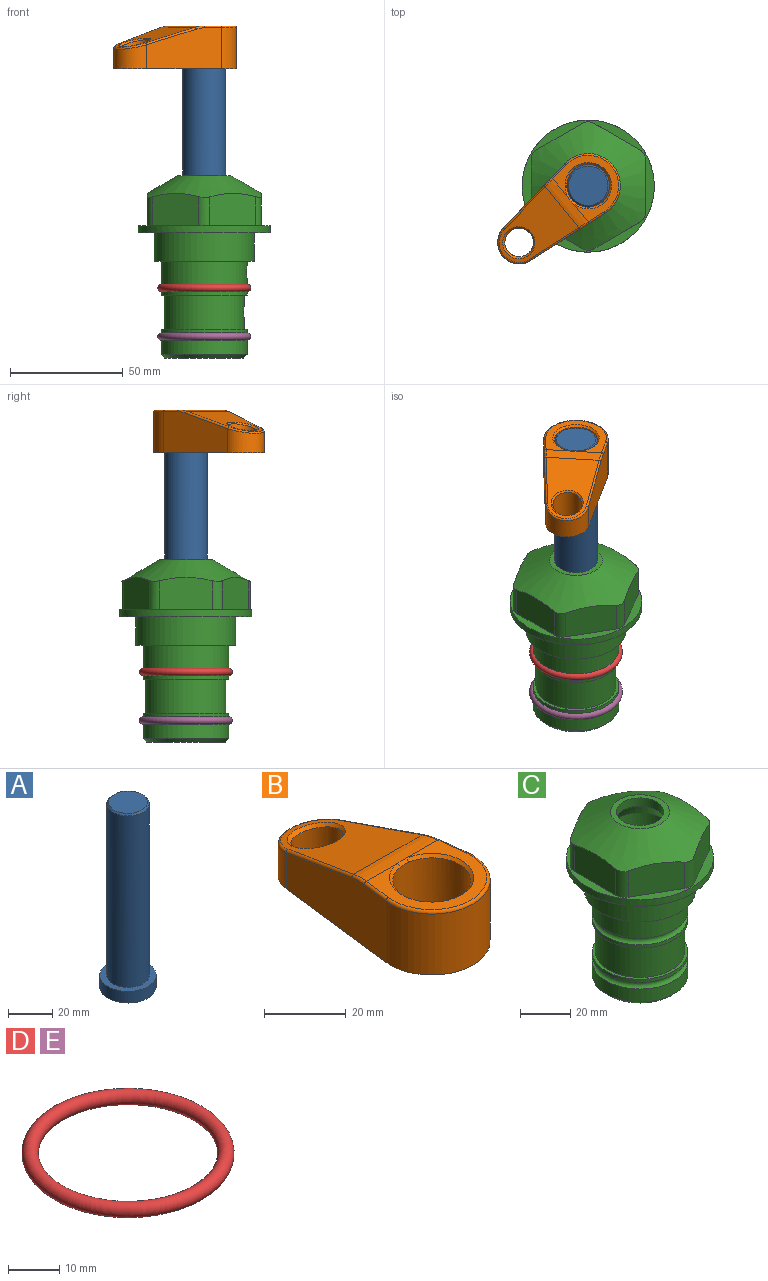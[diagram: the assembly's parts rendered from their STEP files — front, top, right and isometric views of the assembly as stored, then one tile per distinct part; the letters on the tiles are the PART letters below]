
ASSEMBLY  parts=5 mates=4
PART A: 6 faces, bbox 25.4x25.4x101.6 mm
  f0: plane 17.46x17.46mm, normal (0,0,1), area 239.5mm2, adj f5
  f1: plane 25.4x25.4mm, normal (0,0,-1), area 506.7mm2, adj f2
  f2: cylinder r=12.7mm len=25.4mm, axis (0,0,1), area 506.7mm2, adj f1,f3
  f3: plane 25.4x25.4mm, normal (0,0,1), area 221.7mm2, adj f2,f4
  f4: cylinder r=9.53mm len=94.46mm, axis (0,0,1), area 5653mm2, adj f3,f5
  f5: cone r=8.73mm half-angle=45deg, axis (0,0,-1), area 64.4mm2, adj f0,f4
PART B: 31 faces, bbox 31.7x65.5x19.8 mm
  f0: plane 39.12x18.26mm, normal (0.99,0.12,0), area 612.2mm2, adj f1,f4,f7,f11,f13,f15
  f1: cylinder r=9.53mm len=18.91mm, axis (0,0,-1), area 296.1mm2, adj f0,f2,f7,f17
  f2: plane 39.12x18.26mm, normal (-0.99,0.12,0), area 612.2mm2, adj f1,f4,f7,f12,f14,f16
  f3: cylinder r=6.35mm len=12.7mm, axis (0,0,-1), area 362.4mm2, adj f7,f18
  f4: cylinder r=14.29mm len=28.58mm, axis (0,0,-1), area 882.2mm2, adj f0,f2,f7,f10
  f5: cylinder r=9.53mm len=19.05mm, axis (0,0,-1), area 1092.6mm2, adj f7,f19,f20
  f6: plane 26.99x23.69mm, normal (0,0,1), area 216.2mm2, adj f9,f10,f11,f12,f19
  f7: plane 63.5x28.58mm, normal (0,0,-1), area 661.8mm2, adj f0,f1,f2,f3,f4,f5,f22,f23
  f8: plane 33.52x23.6mm, normal (0,0.26,0.97), area 486mm2, adj f9,f15,f16,f17,f18
  f9: cylinder r=19.05mm len=24.72mm, axis (1,0,0), area 120.4mm2, adj f6,f8,f13,f14,f20
  f10: torus R=13.49mm, axis (0,0,1), area 59mm2, adj f4,f6,f11,f12
  f11: cylinder r=0.79mm len=8.67mm, axis (0.12,-0.99,0), area 10.8mm2, adj f0,f6,f10,f13
  f12: cylinder r=0.79mm len=8.67mm, axis (0.12,0.99,0), area 10.8mm2, adj f2,f6,f10,f14
  f13: bspline ~4.95x1.42mm, area 6.1mm2, adj f0,f9,f11,f15
  f14: bspline ~4.95x1.42mm, area 6.1mm2, adj f2,f9,f12,f16
  f15: cylinder r=0.79mm len=25.95mm, axis (0.12,-0.96,0.26), area 32.9mm2, adj f0,f8,f13,f17
  f16: cylinder r=0.79mm len=25.95mm, axis (0.12,0.96,-0.26), area 32.9mm2, adj f2,f8,f14,f17
  f17: bspline ~18.91x8.38mm, area 30mm2, adj f1,f8,f15,f16
  f18: bspline ~14.29x14.29mm, area 48.3mm2, adj f3,f8
  f19: cone r=9.53mm half-angle=45deg, axis (0,0,1), area 66.5mm2, adj f5,f6,f20
  f20: bspline ~3.22x0.96mm, area 3.5mm2, adj f5,f9,f19
  f21: plane 2.75x2.72mm, normal (0,0,-1), area 2.9mm2, adj f23,f25,f28
  f22: plane 23.05x15.88mm, normal (-0.99,-0.12,0), area 323.6mm2, adj f7,f25,f26,f27,f28,f29
  f23: plane 23.05x15.88mm, normal (0.99,-0.12,0), area 323.6mm2, adj f7,f21,f25,f27,f28,f30
  f24: cylinder r=9.53mm len=10.69mm, axis (0,0,-1), area 114.7mm2, adj f7,f27,f29,f30
  f25: cylinder r=12.7mm len=20.59mm, axis (0,0,-1), area 381.1mm2, adj f7,f21,f22,f23,f26,f28
  f26: plane 2.75x2.72mm, normal (0,0,-1), area 2.9mm2, adj f22,f25,f28
  f27: plane 19.72x18.37mm, normal (0,-0.26,-0.97), area 291.8mm2, adj f22,f23,f24,f28,f29,f30
  f28: cylinder r=15.88mm len=19.92mm, axis (1,0,0), area 54.8mm2, adj f21,f22,f23,f25,f26,f27
  f29: cylinder r=1.59mm len=11mm, axis (0,0,-1), area 34.7mm2, adj f7,f22,f24,f27
  f30: cylinder r=1.59mm len=11mm, axis (0,0,-1), area 34.7mm2, adj f7,f23,f24,f27
PART C: 36 faces, bbox 58.7x58.7x81 mm
  f0: cylinder r=17.78mm len=35.56mm, axis (0,0,1), area 1670.8mm2, adj f23,f24,f31
  f1: cylinder r=19.05mm len=38.1mm, axis (0,0,1), area 1191.9mm2, adj f26,f27,f30
  f2: plane 58.66x58.66mm, normal (0,0,-1), area 1150.6mm2, adj f3,f28
  f3: cylinder r=29.33mm len=58.66mm, axis (0,0,-1), area 585.1mm2, adj f2,f4
  f4: plane 58.66x58.66mm, normal (0,0,1), area 475.9mm2, adj f3,f5,f6,f7,f8,f9,f10,f11
  f5: plane 20.32x14.34mm, normal (-0.5,0.87,0), area 324.4mm2, adj f4,f15,f16,f17
  f6: plane 20.32x14.34mm, normal (0.5,0.87,0), area 324.4mm2, adj f4,f14,f15,f17
  f7: plane 23.48x14.34mm, normal (1,0,0), area 324.4mm2, adj f4,f13,f14,f17
  f8: plane 20.32x14.34mm, normal (0.5,-0.87,0), area 324.4mm2, adj f4,f12,f13,f17
  f9: plane 20.32x14.34mm, normal (-0.5,-0.87,0), area 324.4mm2, adj f4,f11,f12,f17
  f10: plane 23.48x14.34mm, normal (-1,0,0), area 324.4mm2, adj f4,f11,f16,f17
  f11: cylinder r=5.08mm len=12.85mm, axis (0,0,-1), area 67.2mm2, adj f4,f9,f10,f17
  f12: cylinder r=5.08mm len=12.85mm, axis (0,0,-1), area 67.2mm2, adj f4,f8,f9,f17
  f13: cylinder r=5.08mm len=12.85mm, axis (0,0,-1), area 67.2mm2, adj f4,f7,f8,f17
  f14: cylinder r=5.08mm len=12.85mm, axis (0,0,-1), area 67.2mm2, adj f4,f6,f7,f17
  f15: cylinder r=5.08mm len=12.85mm, axis (0,0,-1), area 67.2mm2, adj f4,f5,f6,f17
  f16: cylinder r=5.08mm len=12.85mm, axis (0,0,-1), area 67.2mm2, adj f4,f5,f10,f17
  f17: cone r=11.73mm half-angle=60deg, axis (0,0,-1), area 2071.8mm2, adj f5,f6,f7,f8,f9,f10,f11,f12
  f18: plane 23.46x23.46mm, normal (0,0,1), area 147.4mm2, adj f17,f35
  f19: plane 34.93x34.93mm, normal (0,0,-1), area 958mm2, adj f29
  f20: cylinder r=19.05mm len=38.1mm, axis (0,0,1), area 760.1mm2, adj f21,f29
  f21: torus R=19.05mm, axis (0,0,1), area 565.3mm2, adj f20,f22
  f22: cylinder r=19.05mm len=38.1mm, axis (0,0,1), area 190mm2, adj f21,f23
  f23: plane 38.1x38.1mm, normal (0,0,1), area 146.9mm2, adj f0,f22
  f24: plane 38.1x38.1mm, normal (0,0,-1), area 146.9mm2, adj f0,f25
  f25: cylinder r=19.05mm len=38.1mm, axis (0,0,1), area 190mm2, adj f24,f26
  f26: torus R=19.05mm, axis (0,0,1), area 565.3mm2, adj f1,f25
  f27: plane 44.45x44.45mm, normal (0,0,-1), area 411.7mm2, adj f1,f28
  f28: cylinder r=22.23mm len=44.45mm, axis (0,0,1), area 1773.5mm2, adj f2,f27
  f29: cone r=19.05mm half-angle=45deg, axis (0,0,1), area 257.5mm2, adj f19,f20
  f30: cylinder r=3.17mm len=6.75mm, axis (-1,0,0), area 128mm2, adj f1,f33
  f31: cylinder r=3.17mm len=6.35mm, axis (-1,0,0), area 102.5mm2, adj f0,f33
  f32: plane 25.4x25.4mm, normal (0,0,1), area 506.7mm2, adj f33
  f33: cylinder r=12.7mm len=66.42mm, axis (0,0,-1), area 5236.2mm2, adj f30,f31,f32,f34
  f34: cone r=9.53mm half-angle=30deg, axis (0,0,-1), area 443.4mm2, adj f33,f35
  f35: cylinder r=9.53mm len=19.05mm, axis (0,0,-1), area 240.9mm2, adj f18,f34
PART D: 1 faces, bbox 44.7x44.7x3.2 mm
  f0: torus R=19.05mm, axis (0,0,1), area 1193.9mm2
PART E: same geometry as D
PLACE A rot(axis=(0,0,1),129.4deg) t=(0,0,27.55)mm
PLACE B rot(axis=(0,0,1),129.4deg) t=(0,0,28.35)mm
PLACE C at identity fixed
PLACE D at identity
PLACE E t=(0,0,-21.59)mm
MATE fastened D.f0 <-> C.f0  axis (0,0,1) through (0,0,-24.51)mm
MATE fastened E.f0 <-> C.f0  axis (0,0,1) through (0,0,-46.1)mm
MATE fastened B.f4 <-> A.f2  axis (0,0,1) through (0,0,91.05)mm
MATE cylindrical A.f2 <-> C.f0  axis (0,0,-1) through (0,0,-10.55)mm
